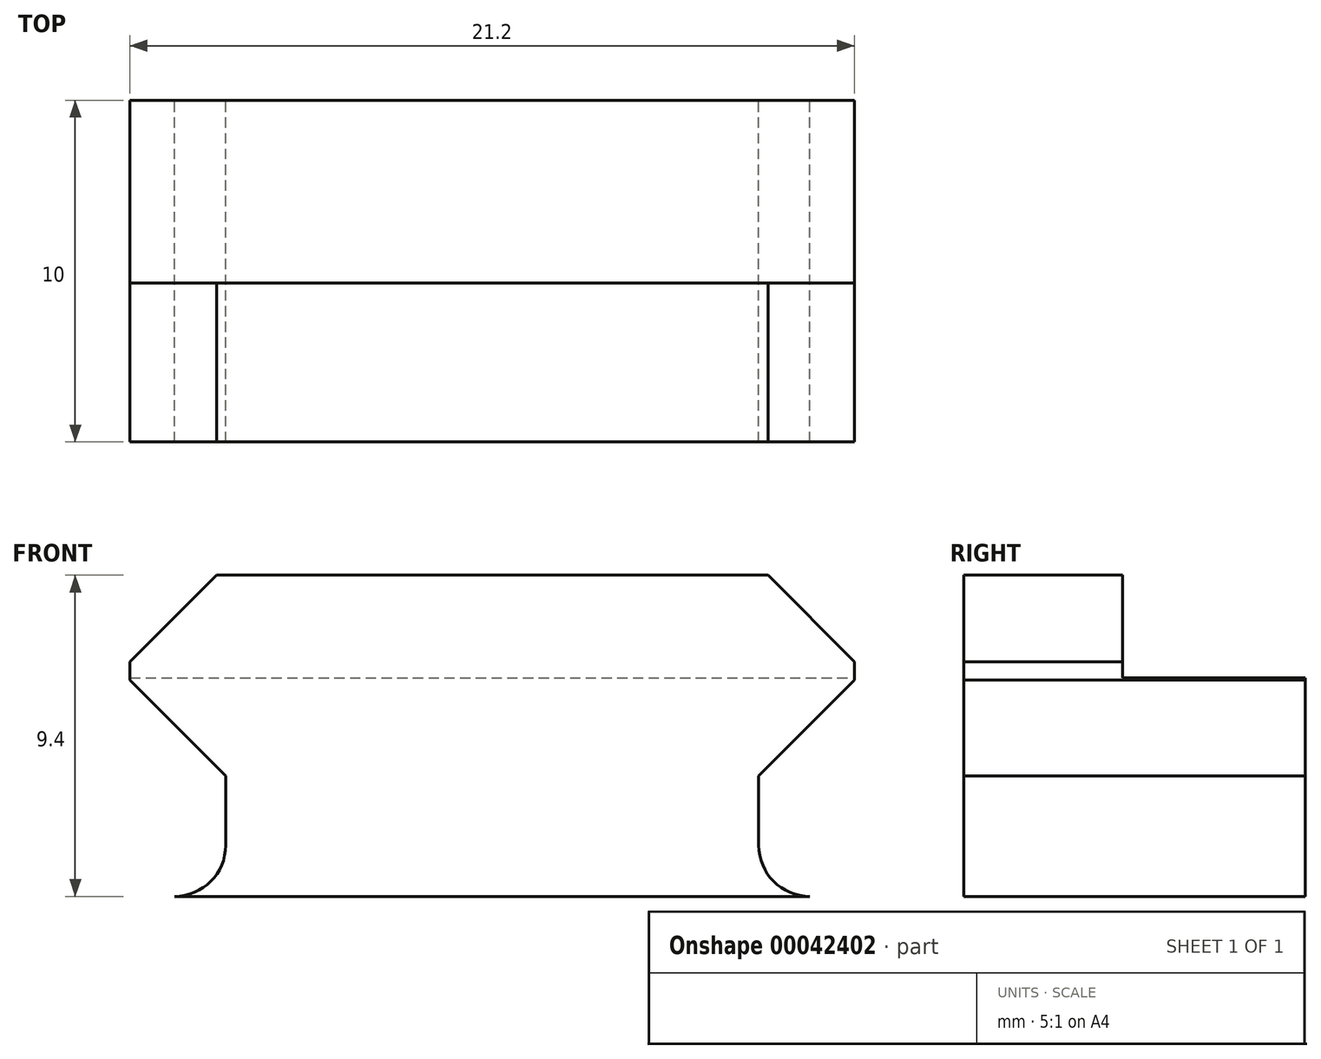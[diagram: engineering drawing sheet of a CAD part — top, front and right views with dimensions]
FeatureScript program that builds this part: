
annotation { "Feature Type Name" : "Feature", "Feature Type Description" : "" }
export const myFeature = defineFeature(function(context is Context, id is Id, definition is map)
    precondition{}
    {
        {
            var Q0;
            Q0=qCreatedBy(makeId("Front.planeOp"),FACE);
            var sketch = newSketch(context, id + "F0", { "sketchPlane" : qUnion([Q0])});
            skLineSegment(sketch, "E0", {"start": v(-10.6, -2.8) * mm, "end": v(10.6, -2.8) * mm, "construction": true});
            skLineSegment(sketch, "E1", {"start": v(-10.6, -3.07) * mm, "end": v(-10.6, -2.53) * mm});
            skLineSegment(sketch, "E2", {"start": v(-10.6, -2.53) * mm, "end": v(-8.07, 0) * mm});
            skLineSegment(sketch, "E3", {"start": v(-8.07, 0) * mm, "end": v(8.07, 0) * mm});
            skLineSegment(sketch, "E4", {"start": v(8.07, 0) * mm, "end": v(10.6, -2.53) * mm});
            skLineSegment(sketch, "E5", {"start": v(10.6, -2.53) * mm, "end": v(10.6, -3.07) * mm});
            skLineSegment(sketch, "E6", {"start": v(10.6, -3.07) * mm, "end": v(7.8, -5.87) * mm});
            skLineSegment(sketch, "E7", {"start": v(7.8, -5.87) * mm, "end": v(7.8, -7.9) * mm});
            skLineSegment(sketch, "E8", {"start": v(-7.8, -7.9) * mm, "end": v(-7.8, -5.87) * mm});
            skLineSegment(sketch, "E9", {"start": v(-7.8, -5.87) * mm, "end": v(-10.6, -3.07) * mm});
            skLineSegment(sketch, "E10", {"start": v(0, 0) * mm, "end": v(0, -9.4) * mm, "construction": true});
            skLineSegment(sketch, "E11", {"start": v(-8.07, 0) * mm, "end": v(-17.76, 0) * mm, "construction": true});
            skLineSegment(sketch, "E12", {"start": v(8.07, 0) * mm, "end": v(18.28, 0) * mm, "construction": true});
            skLineSegment(sketch, "E13", {"start": v(7.8, -9.4) * mm, "end": v(7.8, 0) * mm, "construction": true});
            skLineSegment(sketch, "E14", {"start": v(-9.5, -4.17) * mm, "end": v(9.5, -4.17) * mm, "construction": true});
            skLineSegment(sketch, "E15", {"start": v(9.5, -1.43) * mm, "end": v(-9.5, -1.43) * mm, "construction": true});
            skLineSegment(sketch, "E16", {"start": v(-9.5, -1.43) * mm, "end": v(-9.5, -4.17) * mm, "construction": true});
            skLineSegment(sketch, "E17", {"start": v(9.5, -1.43) * mm, "end": v(9.5, -4.17) * mm, "construction": true});
            skLineSegment(sketch, "E18", {"start": v(9.5, -4.17) * mm, "end": v(9.5, 0) * mm, "construction": true});
            skPoint(sketch, "E19.visualSharp", {"position": v(-7.8, -9.4) * mm});
            skArc(sketch, "E19.filletArc", {"start": v(-9.3, -9.4) * mm, "mid": v(-8.24, -8.96) * mm, "end": v(-7.8, -7.9) * mm});
            skPoint(sketch, "E20.visualSharp", {"position": v(7.8, -9.4) * mm});
            skArc(sketch, "E20.filletArc", {"start": v(7.8, -7.9) * mm, "mid": v(8.24, -8.96) * mm, "end": v(9.3, -9.4) * mm});
            skLineSegment(sketch, "E21", {"start": v(-7.8, -5.87) * mm, "end": v(7.8, -5.87) * mm, "construction": true});
            skLineSegment(sketch, "E22", {"start": v(-9.3, -9.4) * mm, "end": v(9.3, -9.4) * mm});
            skPoint(sketch, "E23", {"position": v(0, -9.4) * mm});
            skSolve(sketch);
        }
        {
            var Q0;
            Q0 = qSketchRegion(id + "F0", true);
            extrude(context, id + "F1", {"entities" : qUnion([Q0]), "depth" : 10 * mm});
        }
        {
            var Q0;
            Q0=qCreatedBy(makeId("Front.planeOp"),FACE);
            var sketch = newSketch(context, id + "F2", { "sketchPlane" : qUnion([Q0])});
            skLineSegment(sketch, "E24.bottom", {"start": v(-10.6, 0) * mm, "end": v(10.6, 0) * mm});
            skLineSegment(sketch, "E24.top", {"start": v(-10.6, -3) * mm, "end": v(10.6, -3) * mm});
            skLineSegment(sketch, "E24.left", {"start": v(-10.6, 0) * mm, "end": v(-10.6, -3) * mm});
            skLineSegment(sketch, "E24.right", {"start": v(10.6, 0) * mm, "end": v(10.6, -3) * mm});
            skSolve(sketch);
        }
        {
            var Q0;
            Q0 = qSketchRegion(id + "F2", true);
            extrude(context, id + "F3", {"entities" : qUnion([Q0]), "depth" : 5.35 * mm});
        }
        {
            var Q0;
            Q0=makeQuery(id+"F3.opExtrude","SWEPT_BODY",BODY,{"disambiguationData":[OSD([sQuery(id+"F2.wireOp",EDGE,"E24.bottom"),sQuery(id+"F2.wireOp",EDGE,"E24.top"),sQuery(id+"F2.wireOp",EDGE,"E24.left"),sQuery(id+"F2.wireOp",EDGE,"E24.right")])]});
            var Q1;
            Q1=makeQuery(id+"F1.opExtrude","SWEPT_BODY",BODY,{"disambiguationData":[OSD([sQuery(id+"F0.wireOp",EDGE,"E1"),sQuery(id+"F0.wireOp",EDGE,"E2"),sQuery(id+"F0.wireOp",EDGE,"E3"),sQuery(id+"F0.wireOp",EDGE,"E4"),sQuery(id+"F0.wireOp",EDGE,"E5"),sQuery(id+"F0.wireOp",EDGE,"E6"),sQuery(id+"F0.wireOp",EDGE,"E7"),sQuery(id+"F0.wireOp",EDGE,"e10688d7-d44b-45e1-9e71-2647d0456736"),sQuery(id+"F0.wireOp",EDGE,"E8"),sQuery(id+"F0.wireOp",EDGE,"E9"),sQuery(id+"F0.wireOp",EDGE,"2f4cb75b-9706-459d-b0f4-f115e851ccbf"),sQuery(id+"F0.wireOp",EDGE,"df6414be-d73f-43e8-8583-a914b0e8a38a"),sQuery(id+"F0.wireOp",EDGE,"4a54f7f0-58ab-4d26-8cd5-d45017e30607"),sQuery(id+"F0.wireOp",EDGE,"fbdd3cc0-3aed-4f7b-98fb-14e2ed6d7a8c"),sQuery(id+"F0.wireOp",EDGE,"E19.filletArc"),sQuery(id+"F0.wireOp",EDGE,"E20.filletArc")])]});
            booleanBodies(context, id + "F4", {"operationType" : BooleanOperationType.SUBTRACTION, "tools" : qUnion([Q0]), "targets" : qUnion([Q1])});
        }
    });
